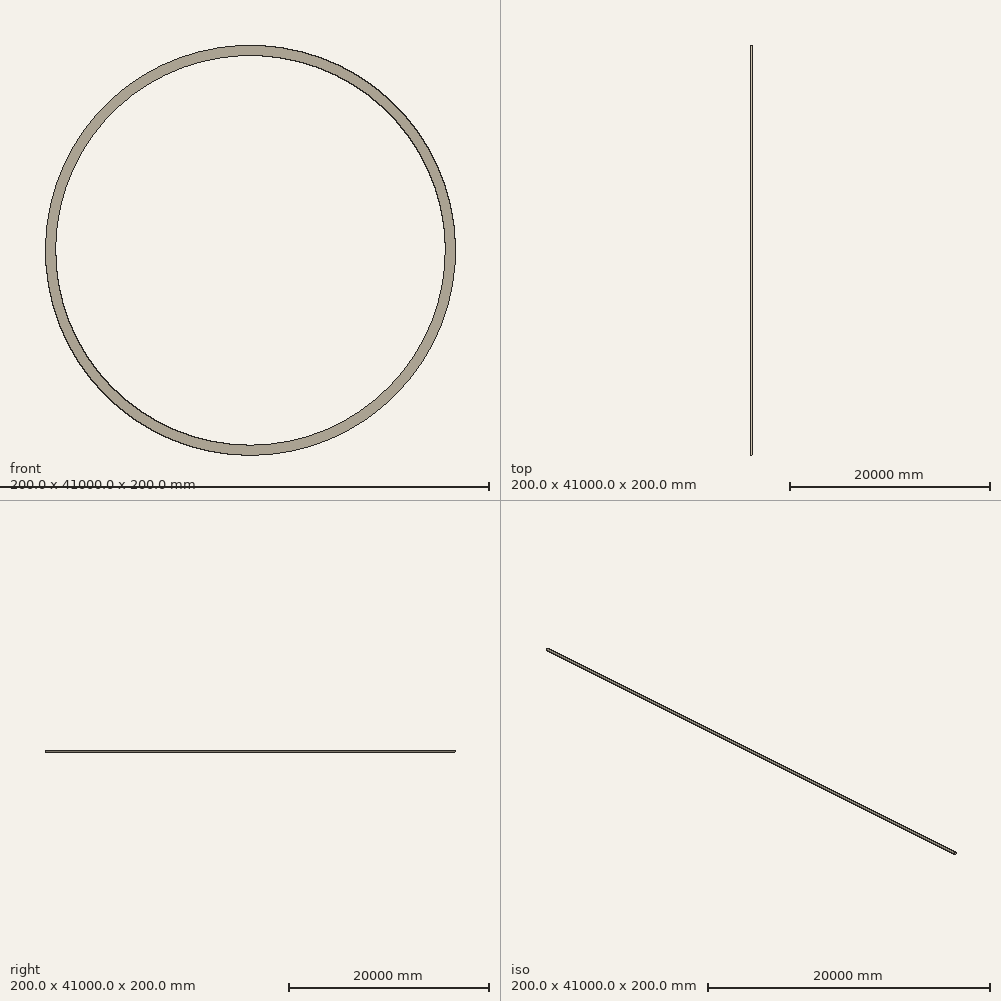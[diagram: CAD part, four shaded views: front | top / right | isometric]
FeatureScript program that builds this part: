
annotation { "Feature Type Name" : "Feature", "Feature Type Description" : "" }
export const myFeature = defineFeature(function(context is Context, id is Id, definition is map)
    precondition{}
    {
        {
            var Q0;
            Q0=qCreatedBy(makeId("Front.planeOp"),FACE);
            var sketch = newSketch(context, id + "F0", { "sketchPlane" : qUnion([Q0])});
            skCircle(sketch, "E0", {"center": v(0, 0) * mm, "radius": 100 * mm});
            skCircle(sketch, "E1", {"center": v(0, 0) * mm, "radius": 95 * mm});
            skSolve(sketch);
        }
        {
            var Q0;
            Q0=makeQuery(id+"F0.imprint","IMPRINT",FACE,{"disambiguationData":[TD([[makeQuery(id+"F0.imprint","IMPRINT",EDGE,{"derivedFrom":sQuery(id+"F0.wireOp",EDGE,"E0")}),1.0]])]});
            extrude(context, id + "F1", {"entities" : qUnion([Q0]), "endBound" : BoundingType.SYMMETRIC, "depth" : 41000 * mm, "offsetDistance" : 25 * mm});
        }
    });
